# Revit family: Toilet_Seat-Elongated_Closed_Front-KOHLER-Saile-K-4141T_1
name_source: partatom
category: Specialty Equipment
units: mm (PartAtom-declared; Revit-internal decimal feet)

## family parameters
Cut with Voids When Loaded = No
Host = Face
OmniClass Number = 23.31.19.19.17
Part Type = Normal
Room Calculation Point = No
Round Connector Dimension = Use Diameter
Shared = No

## types (4) — shared parameters
ADA Compliant = No
Assembly Code = C1030200
Date Modified = 14/03/2024
Default Elevation = 15"
Height = 2 1/16"
Length = 19 11/16"
Manufacturer = Kohler Co.
Master Format 2014 = 10 28 00
Master Format 2014 Name = Toilet, Bath, and Laundry Accessories
Material = Plastic
Product Name = Saile
URL = http://www.kohler.com.cn
WaterSense Certified = No
Width = 14 3/8"

## per-type parameters (varying)
| type | Description | Finish | Model | Product Documentation Link | Product Page URL | Type |
| 0-White | VEILVIA Level 5 Cyclone Green Energy split toilet | Kohler-Plastic-0-White | K-4141T-0 | https://files.kohler.com.cn | https://www.kohler.com.cn | 1 |
| 7-Black Black | VEILVIA Level 5 Cyclone Green Energy split toilet | Kohler-Plastic-7-Black_Black | K-4141T-7 | https://files.kohler.com.cn |  | 2 |
| 2P, 0-White | Quiet Close Toilet Seat | Kohler-Plastic-0-White | K-4141T-2P-0 |  |  | 3 |
| 2PM.0-White | Quiet Close Toilet Seat, Hidden Hinge Base | Kohler-Plastic-0-White | K-4141T-2PM-0 |  |  | 4 |

## geometry (parser evidence)
native form markers: Sweep x4
no freeform markers — native parametric forms only
